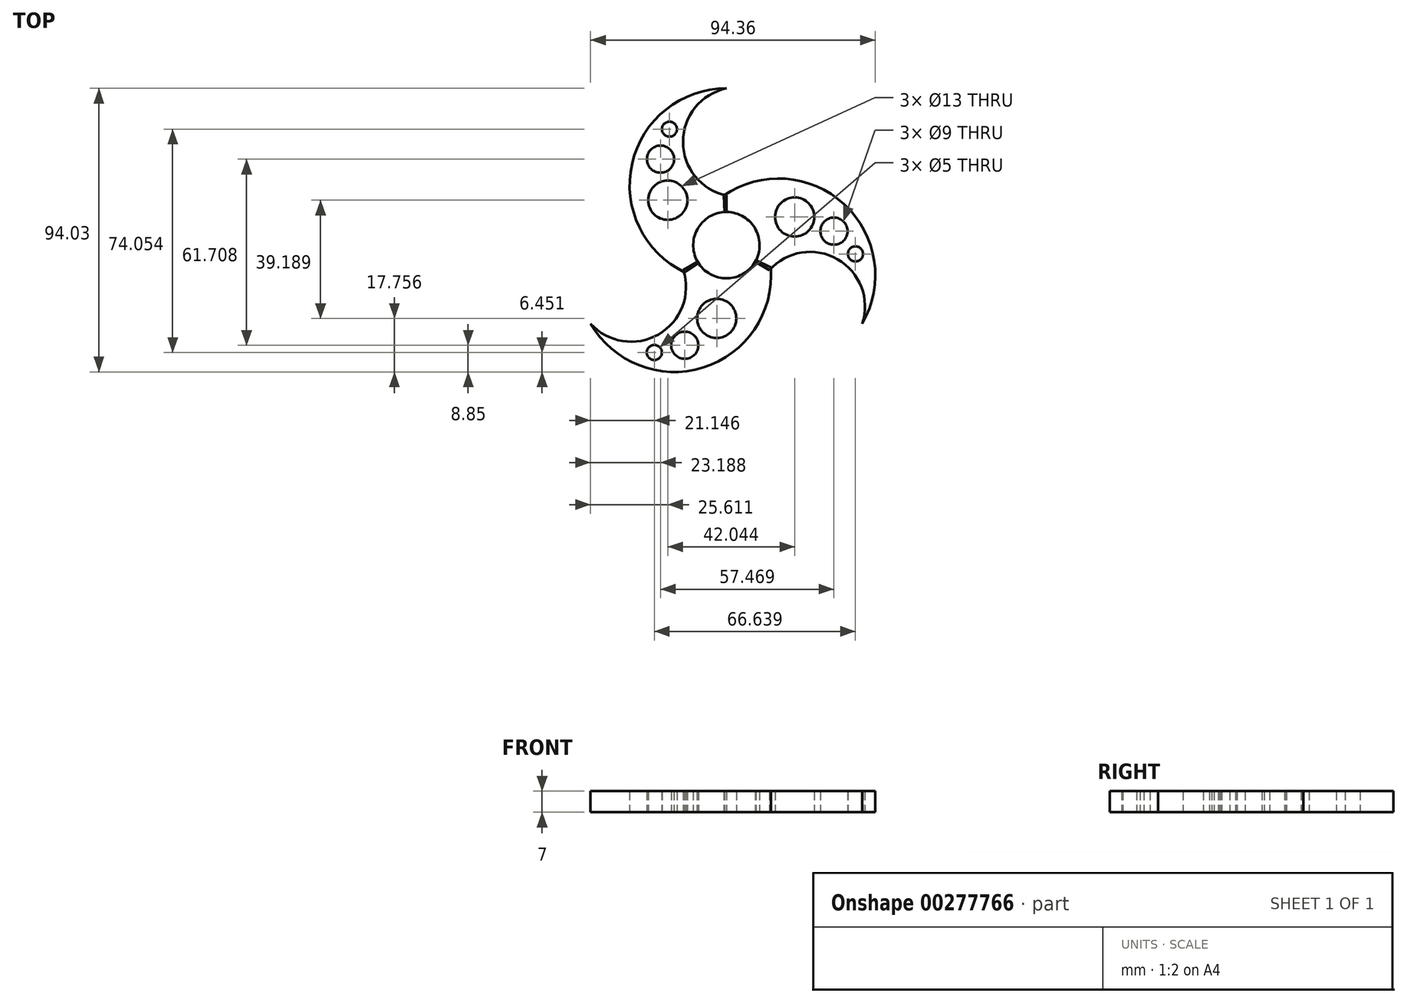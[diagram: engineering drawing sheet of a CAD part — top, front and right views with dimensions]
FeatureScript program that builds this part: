
annotation { "Feature Type Name" : "Feature", "Feature Type Description" : "" }
export const myFeature = defineFeature(function(context is Context, id is Id, definition is map)
    precondition{}
    {
        {
            var Q0;
            Q0=qCreatedBy(makeId("Top.planeOp"),FACE);
            var sketch = newSketch(context, id + "F0", { "sketchPlane" : qUnion([Q0])});
            skCircle(sketch, "E0", {"center": v(0, 0) * mm, "radius": 11 * mm});
            skCircle(sketch, "E1", {"center": v(0, 0) * mm, "radius": 4 * mm});
            skCircle(sketch, "E2.0", {"center": v(0, 0) * mm, "radius": 16.48 * mm});
            skLineSegment(sketch, "E3", {"start": v(-13.8, -9.01) * mm, "end": v(0, 0) * mm});
            skLineSegment(sketch, "E4", {"start": v(0, 16.48) * mm, "end": v(0, 0) * mm});
            skPoint(sketch, "E5.trimOffspring.end.orphan", {"position": v(0, 16.48) * mm});
            skArc(sketch, "E6", {"start": v(0, 52) * mm, "mid": v(-31.28, 27) * mm, "end": v(-13.8, -9.01) * mm});
            skArc(sketch, "E7", {"start": v(0, 52) * mm, "mid": v(-14.38, 34.24) * mm, "end": v(0, 16.48) * mm});
            skSolve(sketch);
        }
        {
            var Q0;
            {var subQ4=sQuery(id+"F0.wireOp",EDGE,"E6");Q0=makeQuery(id+"F0.imprint","IMPRINT",FACE,{"disambiguationData":[TD([[makeQuery(id+"F0.imprint","IMPRINT",EDGE,{"derivedFrom":subQ4}),1.0]])]});}
            var Q1;
            {var subQ0=sQuery(id+"F0.wireOp",EDGE,"E3");var subQ1=sQuery(id+"F0.wireOp",EDGE,"E0");var subQ2=makeQuery(id+"F0.imprint","INTERSECT",VERTEX,{"derivedFrom":[subQ1,subQ0]});Q1=makeQuery(id+"F0.imprint","IMPRINT",FACE,{"disambiguationData":[TD([[makeQuery(id+"F0.imprint","IMPRINT",EDGE,{"disambiguationData":[TD([[subQ2,1.0]])],"derivedFrom":subQ1}),-1.0]])]});}
            extrude(context, id + "F1", {"entities" : qUnion([Q0, Q1]), "depth" : 7 * mm});
        }
        {
            var Q0;
            Q0=qCreatedBy(makeId("Top.planeOp"),FACE);
            var sketch = newSketch(context, id + "F2", { "sketchPlane" : qUnion([Q0])});
            skCircle(sketch, "E8", {"center": v(-18.87, 38.47) * mm, "radius": 2.5 * mm});
            skArc(sketch, "E9", {"start": v(0, 52) * mm, "mid": v(-20.64, 34.32) * mm, "end": v(-14.5, 7.85) * mm});
            skCircle(sketch, "E10", {"center": v(-21.84, 28.53) * mm, "radius": 4.5 * mm});
            skCircle(sketch, "E11", {"center": v(-19.42, 14.91) * mm, "radius": 6.5 * mm});
            skSolve(sketch);
        }
        {
            var Q0;
            Q0=qCreatedBy(makeId("Right.planeOp"),FACE);
            var sketch = newSketch(context, id + "F3", { "sketchPlane" : qUnion([Q0])});
            skLineSegment(sketch, "E12", {"start": v(0, 29.24) * mm, "end": v(0, -32.64) * mm, "construction": true});
            skSolve(sketch);
        }
        {
            var Q0;
            Q0 = qSketchRegion(id + "F2", true);
            extrude(context, id + "F4", {"entities" : qUnion([Q0]), "operationType" : NewBodyOperationType.REMOVE, "oppositeDirection" : true, "depth" : 25 * mm});
        }
        {
            var Q0;
            Q0 = qSketchRegion(id + "F2", true);
            extrude(context, id + "F5", {"entities" : qUnion([Q0]), "operationType" : NewBodyOperationType.REMOVE, "oppositeDirection" : true, "depth" : 25 * mm});
        }
        {
            var Q0;
            Q0 = qSketchRegion(id + "F2", true);
            extrude(context, id + "F6", {"entities" : qUnion([Q0]), "operationType" : NewBodyOperationType.REMOVE, "depth" : 25 * mm});
        }
        {
            var Q0;
            Q0=makeQuery(id+"F1.opExtrude","SWEPT_BODY",BODY,{"disambiguationData":[OSD([sQuery(id+"F0.wireOp",EDGE,"E2.0"),sQuery(id+"F0.wireOp",EDGE,"E3"),sQuery(id+"F0.wireOp",EDGE,"E6"),sQuery(id+"F0.wireOp",EDGE,"E7")])]});
            var Q1;
            Q1=sQuery(id+"F3.wireOp",EDGE,"E12");
            circularPattern(context, id + "F7", {"entities" : qUnion([Q0]), "axis" : qUnion([Q1]), "angle" : 360 * degree, "instanceCount" : 3, "equalSpace" : true});
        }
    });
